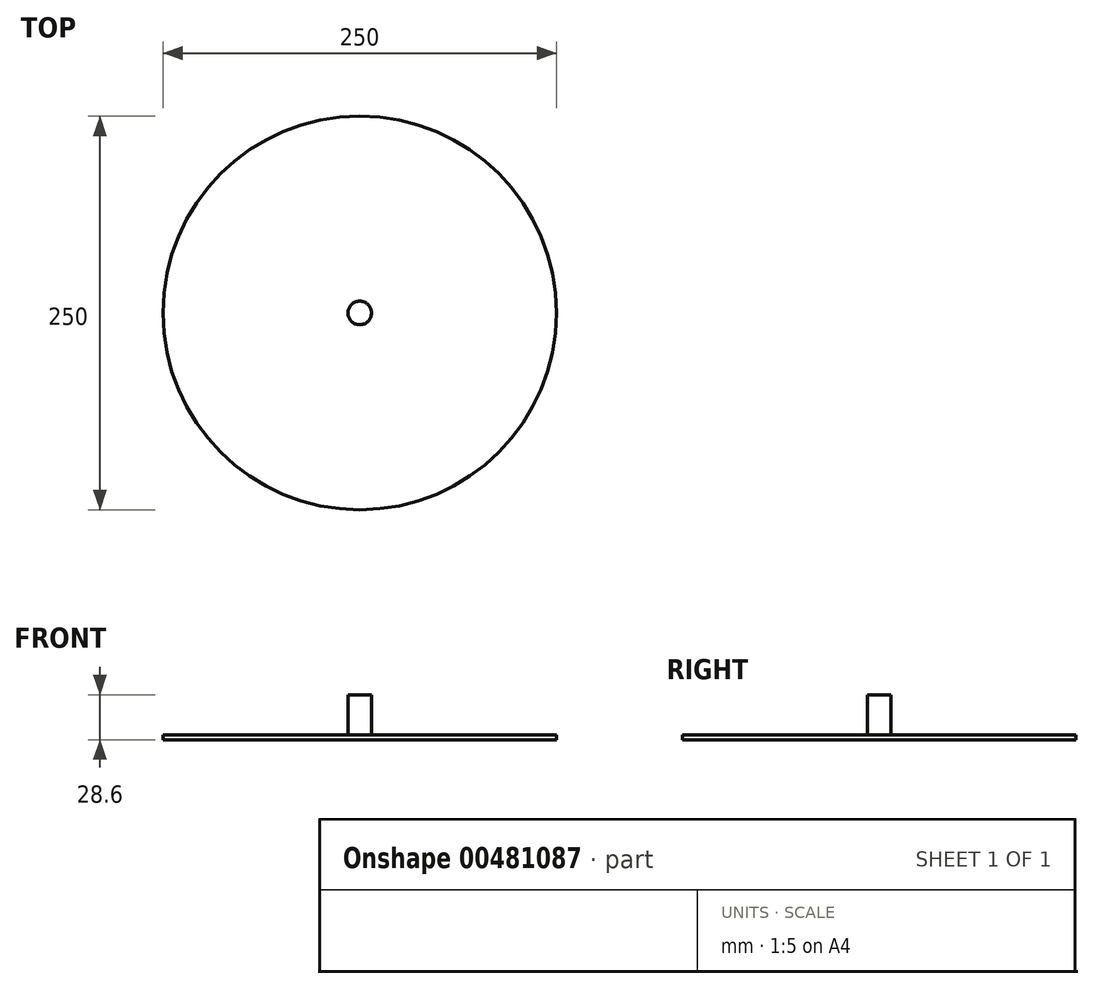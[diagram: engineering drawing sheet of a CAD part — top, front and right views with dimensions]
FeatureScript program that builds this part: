
annotation { "Feature Type Name" : "Feature", "Feature Type Description" : "" }
export const myFeature = defineFeature(function(context is Context, id is Id, definition is map)
    precondition{}
    {
        {
            var Q0;
            Q0=qCreatedBy(makeId("Top.planeOp"),FACE);
            var sketch = newSketch(context, id + "F0", { "sketchPlane" : qUnion([Q0])});
            skCircle(sketch, "E0", {"center": v(0, 0) * mm, "radius": 125 * mm});
            skCircle(sketch, "E1", {"center": v(0, 0) * mm, "radius": 63.5 * mm});
            skText(sketch, "E2", { "text": "Nancy Mazariegos O. 17227\nRonaldo Macz R.          17029\n", "fontName": "Arimo-Regular.ttf"});
            const initialGuessF0  = {"E2": [0.06857, -0.13754, 1, 0, 0.005]};
            skSetInitialGuess(sketch, initialGuessF0);
            skSolve(sketch);
        }
        {
            var Q0;
            Q0=makeQuery(id+"F0.imprint","IMPRINT",FACE,{"disambiguationData":[TD([[makeQuery(id+"F0.imprint","IMPRINT",EDGE,{"derivedFrom":sQuery(id+"F0.wireOp",EDGE,"E0")}),1.0]])]});
            var Q1;
            Q1=makeQuery(id+"F0.imprint","IMPRINT",FACE,{"disambiguationData":[TD([[makeQuery(id+"F0.imprint","IMPRINT",EDGE,{"derivedFrom":sQuery(id+"F0.wireOp",EDGE,"E1")}),1.0]])]});
            extrude(context, id + "F1", {"entities" : qUnion([Q0, Q1]), "depth" : 3.2 * mm});
        }
        {
            var Q0;
            Q0=makeQuery(id+"F1.opExtrude","CAP_FACE",FACE,{"disambiguationData":[OSD([sQuery(id+"F0.wireOp",EDGE,"E0")])],"isStart":false});
            var sketch = newSketch(context, id + "F2", { "sketchPlane" : qUnion([Q0])});
            skCircle(sketch, "E3", {"center": v(0, 0) * mm, "radius": 7.5 * mm});
            skSolve(sketch);
        }
        {
            var Q0;
            Q0=makeQuery(id+"F2.imprint","IMPRINT",FACE,{"disambiguationData":[TD([[makeQuery(id+"F2.imprint","IMPRINT",EDGE,{"derivedFrom":sQuery(id+"F2.wireOp",EDGE,"E3")}),1.0]])]});
            extrude(context, id + "F3", {"entities" : qUnion([Q0]), "operationType" : NewBodyOperationType.ADD, "depth" : 25.4 * mm});
        }
    });
